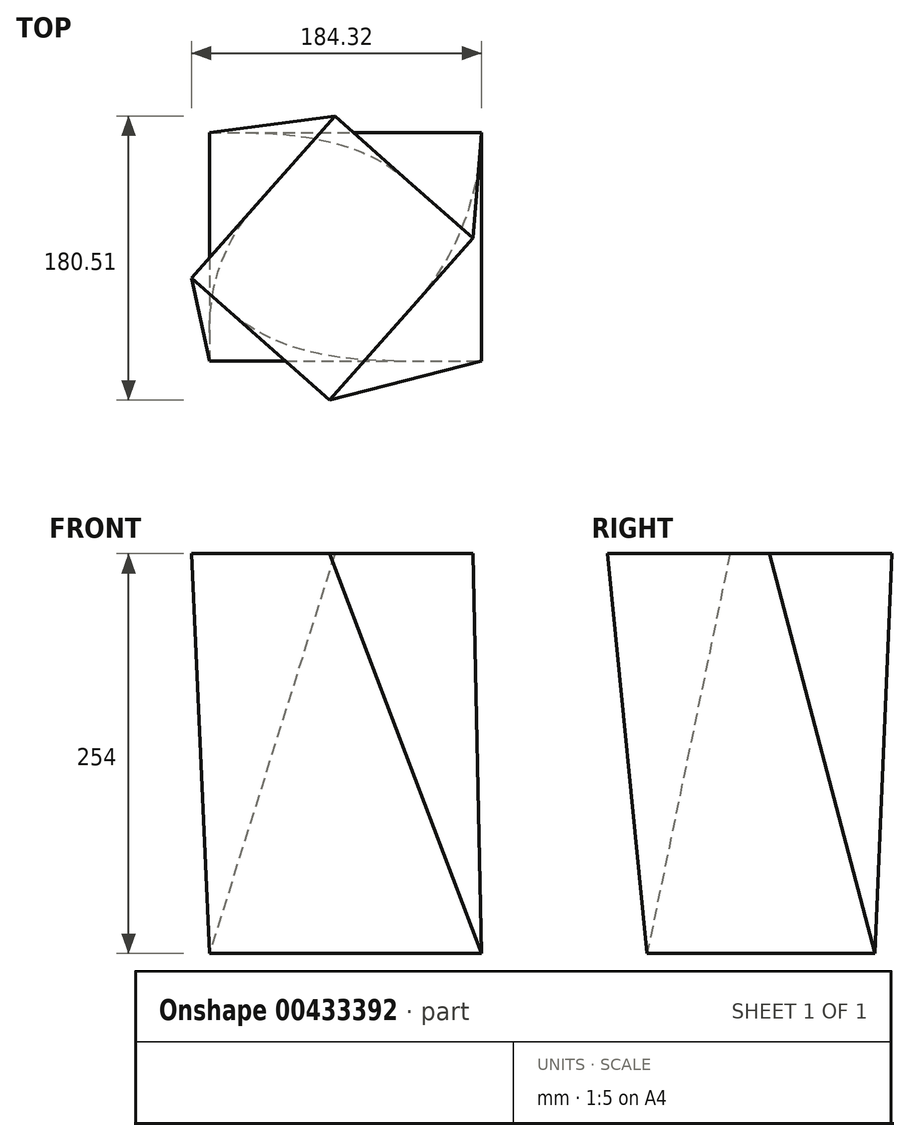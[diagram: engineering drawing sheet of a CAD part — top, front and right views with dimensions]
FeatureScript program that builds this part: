
annotation { "Feature Type Name" : "Feature", "Feature Type Description" : "" }
export const myFeature = defineFeature(function(context is Context, id is Id, definition is map)
    precondition{}
    {
        {
            var Q0;
            Q0=qCreatedBy(makeId("Top.planeOp"),FACE);
            var sketch = newSketch(context, id + "F0", { "sketchPlane" : qUnion([Q0])});
            skLineSegment(sketch, "E0.bottom", {"start": v(-79.65, 69.43) * mm, "end": v(93.32, 69.43) * mm});
            skLineSegment(sketch, "E0.top", {"start": v(-79.65, -75.39) * mm, "end": v(93.32, -75.39) * mm});
            skLineSegment(sketch, "E0.left", {"start": v(-79.65, 69.43) * mm, "end": v(-79.65, -75.39) * mm});
            skLineSegment(sketch, "E0.right", {"start": v(93.32, 69.43) * mm, "end": v(93.32, -75.39) * mm});
            skSolve(sketch);
        }
        {
            var Q0;
            Q0=makeQuery(id+"F0.imprint","IMPRINT",FACE,{"disambiguationData":[TD([[makeQuery(id+"F0.imprint","IMPRINT",EDGE,{"derivedFrom":sQuery(id+"F0.wireOp",EDGE,"E0.bottom")}),-1.0]])]});
            cPlane(context, id + "F1", {"entities" : qUnion([Q0]), "cplaneType" : CPlaneType.OFFSET, "offset" : 254 * mm, "width" : 152.4 * mm, "height" : 152.4 * mm});
        }
        {
            var Q0;
            Q0=qCreatedBy(id+"F1.planeOp",FACE);
            var sketch = newSketch(context, id + "F2", { "sketchPlane" : qUnion([Q0])});
            skLineSegment(sketch, "E1", {"start": v(0, 80.14) * mm, "end": v(-91, -22.67) * mm});
            skLineSegment(sketch, "E2", {"start": v(-91, -22.67) * mm, "end": v(-3.22, -100.37) * mm});
            skLineSegment(sketch, "E3", {"start": v(-3.22, -100.37) * mm, "end": v(87.78, 2.45) * mm});
            skLineSegment(sketch, "E4", {"start": v(87.78, 2.45) * mm, "end": v(0, 80.14) * mm});
            skSolve(sketch);
        }
        {
            var Q0;
            Q0=makeQuery(id+"F2.imprint","IMPRINT",FACE,{"disambiguationData":[TD([[makeQuery(id+"F2.imprint","IMPRINT",EDGE,{"derivedFrom":sQuery(id+"F2.wireOp",EDGE,"E1")}),1.0]])]});
            var Q1;
            Q1=makeQuery(id+"F0.imprint","IMPRINT",FACE,{"disambiguationData":[TD([[makeQuery(id+"F0.imprint","IMPRINT",EDGE,{"derivedFrom":sQuery(id+"F0.wireOp",EDGE,"E0.bottom")}),-1.0]])]});
            loft(context, id + "F3", {"sheetProfilesArray" : [{ "sheetProfileEntities" : qUnion([Q0]) }, { "sheetProfileEntities" : qUnion([Q1]) }]});
        }
    });
